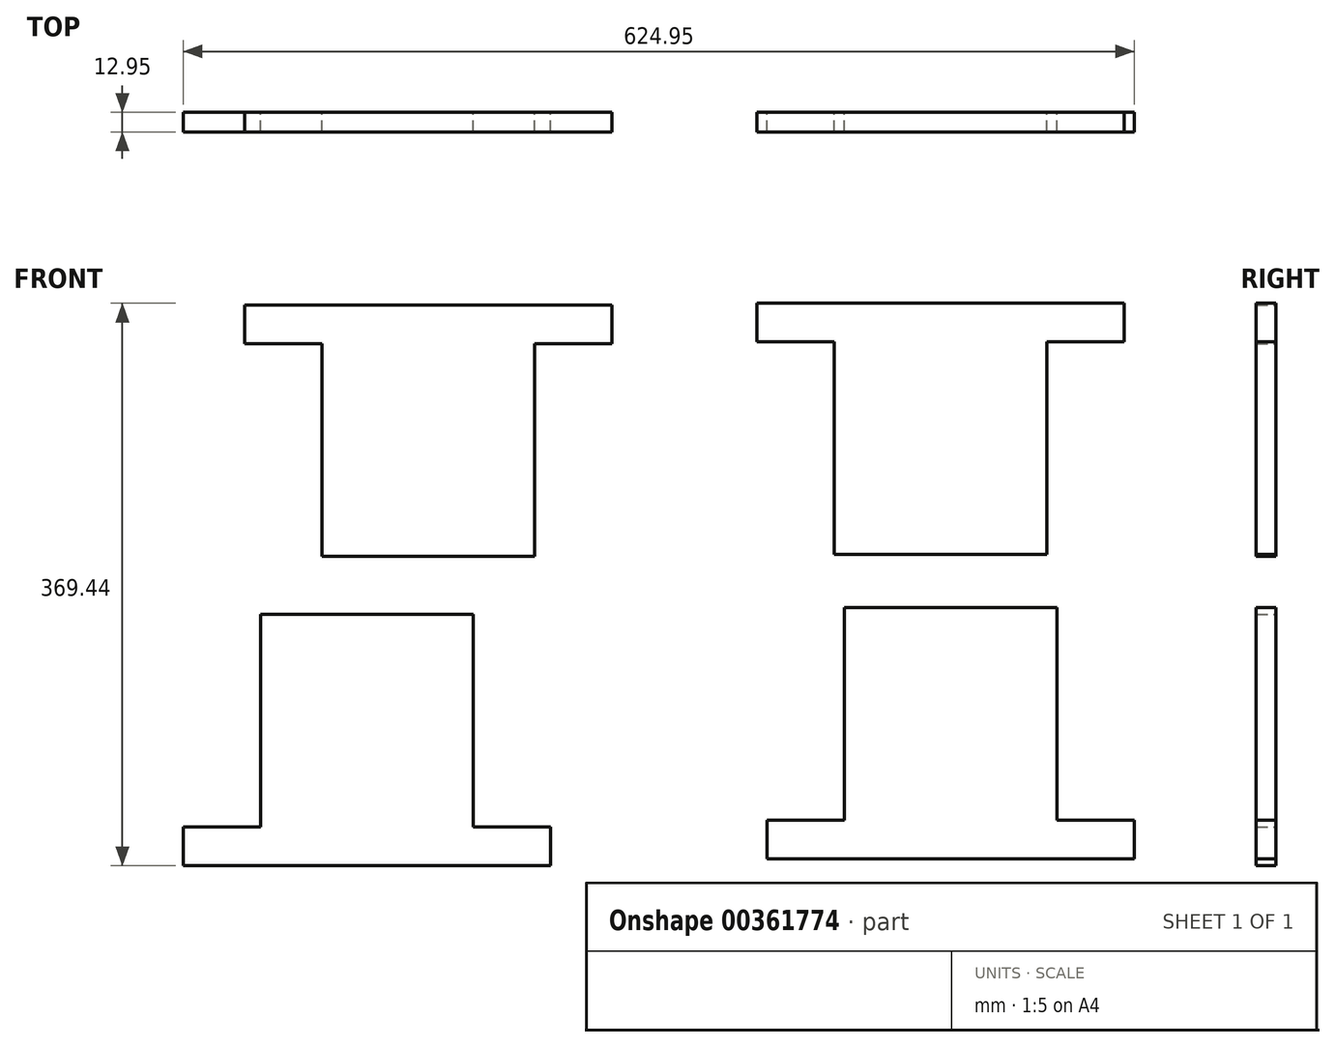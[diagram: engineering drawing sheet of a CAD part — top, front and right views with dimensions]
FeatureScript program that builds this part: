
annotation { "Feature Type Name" : "Feature", "Feature Type Description" : "" }
export const myFeature = defineFeature(function(context is Context, id is Id, definition is map)
    precondition{}
    {
        {
            var Q0;
            Q0=qCreatedBy(makeId("Front.planeOp"),FACE);
            var sketch = newSketch(context, id + "F0", { "sketchPlane" : qUnion([Q0])});
            skLineSegment(sketch, "E0.top", {"start": v(-237.28, 30.64) * mm, "end": v(-97.58, 30.64) * mm});
            skLineSegment(sketch, "E0.left", {"start": v(-237.28, 170.34) * mm, "end": v(-237.28, 30.64) * mm});
            skLineSegment(sketch, "E0.right", {"start": v(-97.58, 170.34) * mm, "end": v(-97.58, 30.64) * mm});
            skLineSegment(sketch, "E1.top", {"start": v(239.02, 31.9) * mm, "end": v(99.32, 31.9) * mm});
            skLineSegment(sketch, "E1.left", {"start": v(239.02, 171.6) * mm, "end": v(239.02, 31.9) * mm});
            skLineSegment(sketch, "E1.right", {"start": v(99.32, 171.6) * mm, "end": v(99.32, 31.9) * mm});
            skLineSegment(sketch, "E2.top", {"start": v(-277.67, -7.34) * mm, "end": v(-137.97, -7.34) * mm});
            skLineSegment(sketch, "E2.left", {"start": v(-277.67, -147.04) * mm, "end": v(-277.67, -7.34) * mm});
            skLineSegment(sketch, "E2.right", {"start": v(-137.97, -147.04) * mm, "end": v(-137.97, -7.34) * mm});
            skLineSegment(sketch, "E3.top", {"start": v(245.68, -3) * mm, "end": v(105.98, -3) * mm});
            skLineSegment(sketch, "E3.left", {"start": v(245.68, -142.7) * mm, "end": v(245.68, -3) * mm});
            skLineSegment(sketch, "E3.right", {"start": v(105.98, -142.7) * mm, "end": v(105.98, -3) * mm});
            skLineSegment(sketch, "E4", {"start": v(99.32, 171.6) * mm, "end": v(48.52, 171.6) * mm});
            skLineSegment(sketch, "E5", {"start": v(239.02, 171.6) * mm, "end": v(289.82, 171.6) * mm});
            skLineSegment(sketch, "E6", {"start": v(48.52, 171.6) * mm, "end": v(48.52, 197) * mm});
            skLineSegment(sketch, "E7", {"start": v(289.82, 171.6) * mm, "end": v(289.82, 197) * mm});
            skLineSegment(sketch, "E8", {"start": v(289.82, 197) * mm, "end": v(48.52, 197) * mm});
            skLineSegment(sketch, "E9", {"start": v(-97.58, 170.34) * mm, "end": v(-46.78, 170.34) * mm});
            skLineSegment(sketch, "E10", {"start": v(-237.28, 170.34) * mm, "end": v(-288.08, 170.34) * mm});
            skLineSegment(sketch, "E11", {"start": v(-288.08, 170.34) * mm, "end": v(-288.08, 195.74) * mm});
            skLineSegment(sketch, "E12", {"start": v(-46.78, 170.34) * mm, "end": v(-46.78, 195.74) * mm});
            skLineSegment(sketch, "E13", {"start": v(-46.78, 195.74) * mm, "end": v(-288.08, 195.74) * mm});
            skLineSegment(sketch, "E14", {"start": v(105.98, -142.7) * mm, "end": v(55.18, -142.7) * mm});
            skLineSegment(sketch, "E15", {"start": v(245.68, -142.7) * mm, "end": v(296.48, -142.7) * mm});
            skLineSegment(sketch, "E16", {"start": v(296.48, -142.7) * mm, "end": v(296.48, -168.1) * mm});
            skLineSegment(sketch, "E17", {"start": v(55.18, -142.7) * mm, "end": v(55.18, -168.1) * mm});
            skLineSegment(sketch, "E18", {"start": v(55.18, -168.1) * mm, "end": v(296.48, -168.1) * mm});
            skLineSegment(sketch, "E19", {"start": v(-277.67, -147.04) * mm, "end": v(-328.47, -147.04) * mm});
            skLineSegment(sketch, "E20", {"start": v(-137.97, -147.04) * mm, "end": v(-87.17, -147.04) * mm});
            skLineSegment(sketch, "E21", {"start": v(-328.47, -147.04) * mm, "end": v(-328.47, -172.44) * mm});
            skLineSegment(sketch, "E22", {"start": v(-87.17, -147.04) * mm, "end": v(-87.17, -172.44) * mm});
            skLineSegment(sketch, "E23", {"start": v(-87.17, -172.44) * mm, "end": v(-328.47, -172.44) * mm});
            skSolve(sketch);
        }
        {
            var Q0;
            Q0=qSketchRegion(id+"F0",true);
            extrude(context, id + "F1", {"entities" : qUnion([Q0]), "depth" : 12.95 * mm});
        }
    });
